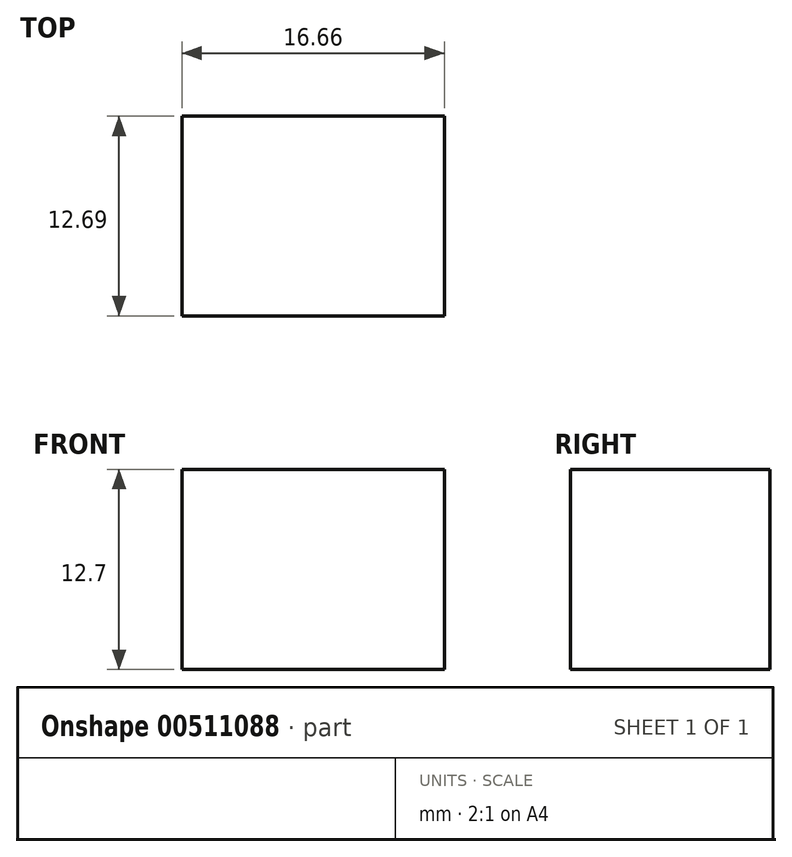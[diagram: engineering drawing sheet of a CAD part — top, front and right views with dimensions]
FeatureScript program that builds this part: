
annotation { "Feature Type Name" : "Feature", "Feature Type Description" : "" }
export const myFeature = defineFeature(function(context is Context, id is Id, definition is map)
    precondition{}
    {
        {
            assignVariable(context, id + "F0", {"name" : "bodyLength", "anyValue" : 14});
        }
        {
            assignVariable(context, id + "F1", {"name" : "thickness", "anyValue" : 0.66});
        }
        {
            var Q0;
            Q0=qCreatedBy(makeId("Front.planeOp"),FACE);
            var sketch = newSketch(context, id + "F2", { "sketchPlane" : qUnion([Q0])});
            skLineSegment(sketch, "E0.bottom", {"start": v(0, 0) * mm, "end": v(16.66, 0) * mm});
            skLineSegment(sketch, "E0.top", {"start": v(0, -12.7) * mm, "end": v(16.66, -12.7) * mm});
            skLineSegment(sketch, "E0.left", {"start": v(0, 0) * mm, "end": v(0, -12.7) * mm});
            skLineSegment(sketch, "E0.right", {"start": v(16.66, 0) * mm, "end": v(16.66, -12.7) * mm});
            skSolve(sketch);
        }
        {
            var Q0;
            Q0=makeQuery(id+"F2.imprint","IMPRINT",FACE,{"disambiguationData":[TD([[makeQuery(id+"F2.imprint","IMPRINT",EDGE,{"derivedFrom":sQuery(id+"F2.wireOp",EDGE,"E0.bottom")}),-1.0]])]});
            extrude(context, id + "F3", {"entities" : qUnion([Q0]), "depth" : (getVariable(context, 'bodyLength') - getVariable(context, 'thickness') * 2) * mm, "offsetDistance" : 25.4 * mm});
        }
    });
